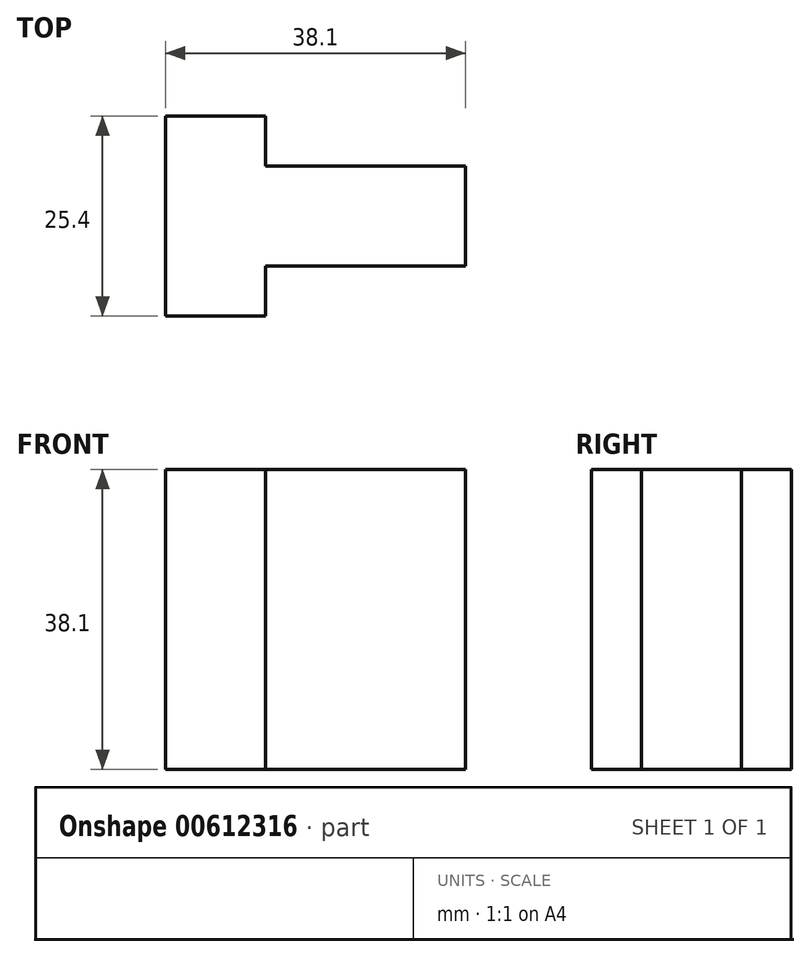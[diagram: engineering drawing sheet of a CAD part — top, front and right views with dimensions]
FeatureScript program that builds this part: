
annotation { "Feature Type Name" : "Feature", "Feature Type Description" : "" }
export const myFeature = defineFeature(function(context is Context, id is Id, definition is map)
    precondition{}
    {
        {
            var Q0;
            Q0=qCreatedBy(makeId("Top.planeOp"),FACE);
            var sketch = newSketch(context, id + "F0", { "sketchPlane" : qUnion([Q0])});
            skLineSegment(sketch, "E0", {"start": v(0, 0) * mm, "end": v(0, 25.4) * mm});
            skLineSegment(sketch, "E1", {"start": v(0, 25.4) * mm, "end": v(12.7, 25.4) * mm});
            skLineSegment(sketch, "E2", {"start": v(12.7, 25.4) * mm, "end": v(12.7, 19.05) * mm});
            skLineSegment(sketch, "E3", {"start": v(12.7, 19.05) * mm, "end": v(38.1, 19.05) * mm});
            skLineSegment(sketch, "E4", {"start": v(38.1, 19.05) * mm, "end": v(38.1, 6.35) * mm});
            skLineSegment(sketch, "E5", {"start": v(38.1, 6.35) * mm, "end": v(12.7, 6.35) * mm});
            skLineSegment(sketch, "E6", {"start": v(12.7, 6.35) * mm, "end": v(12.7, 0) * mm});
            skLineSegment(sketch, "E7", {"start": v(12.7, 0) * mm, "end": v(0, 0) * mm});
            skSolve(sketch);
        }
        {
            var Q0;
            Q0=qSketchRegion(id+"F0",true);
            extrude(context, id + "F1", {"entities" : qUnion([Q0]), "depth" : 38.1 * mm});
        }
    });
